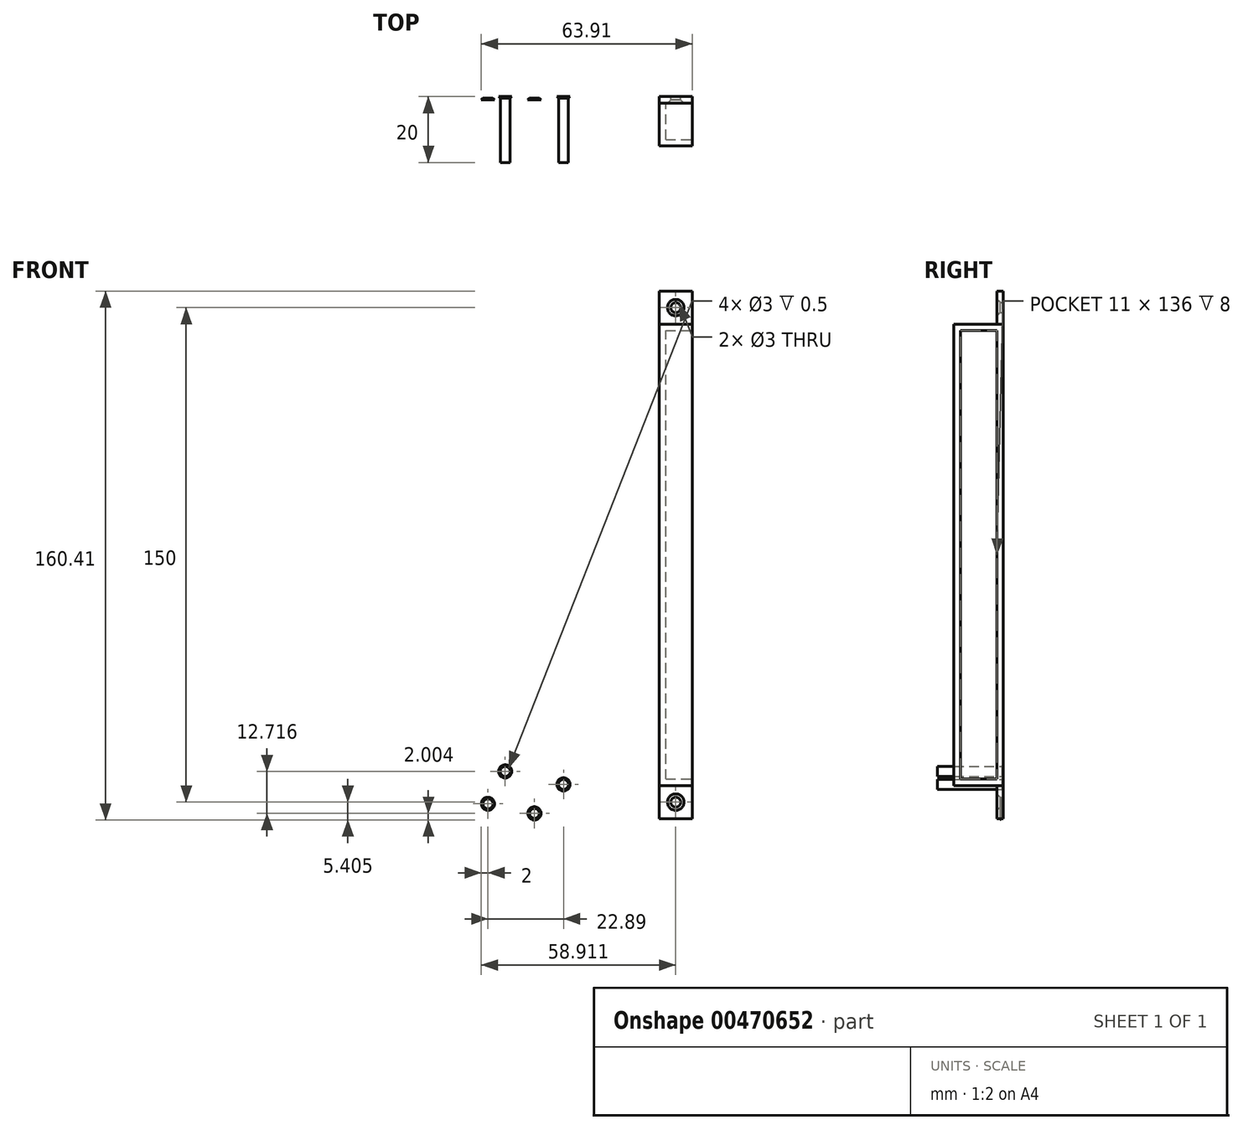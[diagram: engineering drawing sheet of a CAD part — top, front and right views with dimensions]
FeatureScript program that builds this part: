
annotation { "Feature Type Name" : "Feature", "Feature Type Description" : "" }
export const myFeature = defineFeature(function(context is Context, id is Id, definition is map)
    precondition{}
    {
        {
            var Q0;
            Q0=qCreatedBy(makeId("Front.planeOp"),FACE);
            var sketch = newSketch(context, id + "F0", { "sketchPlane" : qUnion([Q0])});
            skLineSegment(sketch, "E0.bottom", {"start": v(-57.99, -14.31) * mm, "end": v(-67.99, -14.31) * mm});
            skLineSegment(sketch, "E0.top", {"start": v(-57.99, 145.69) * mm, "end": v(-67.99, 145.69) * mm});
            skLineSegment(sketch, "E0.left", {"start": v(-57.99, -14.31) * mm, "end": v(-57.99, 145.69) * mm});
            skLineSegment(sketch, "E0.right", {"start": v(-67.99, -14.31) * mm, "end": v(-67.99, 145.69) * mm});
            skPoint(sketch, "E0.middle", {"position": v(-62.99, 65.69) * mm});
            skCircle(sketch, "E1", {"center": v(-62.99, 140.69) * mm, "radius": 1.5 * mm});
            skCircle(sketch, "E2", {"center": v(-62.99, -9.31) * mm, "radius": 1.5 * mm});
            skLineSegment(sketch, "E3", {"start": v(-67.99, -4.31) * mm, "end": v(-57.99, -4.31) * mm});
            skLineSegment(sketch, "E4", {"start": v(-67.99, 135.69) * mm, "end": v(-57.99, 135.69) * mm});
            skSolve(sketch);
        }
        {
            var Q0;
            {var subQ1=sQuery(id+"F0.wireOp",EDGE,"E0.bottom");Q0=makeQuery(id+"F0.imprint","IMPRINT",FACE,{"disambiguationData":[TD([[makeQuery(id+"F0.imprint","IMPRINT",EDGE,{"derivedFrom":subQ1}),-1.0]])]});}
            var Q1;
            {var subQ1=sQuery(id+"F0.wireOp",EDGE,"E0.top");Q1=makeQuery(id+"F0.imprint","IMPRINT",FACE,{"disambiguationData":[TD([[makeQuery(id+"F0.imprint","IMPRINT",EDGE,{"derivedFrom":subQ1}),1.0]])]});}
            extrude(context, id + "F1", {"entities" : qUnion([Q0, Q1]), "depth" : 2 * mm});
        }
        {
            var Q0;
            {var subQ0=sQuery(id+"F0.wireOp",EDGE,"E3");Q0=makeQuery(id+"F0.imprint","IMPRINT",FACE,{"disambiguationData":[TD([[makeQuery(id+"F0.imprint","IMPRINT",EDGE,{"derivedFrom":subQ0}),1.0]])]});}
            extrude(context, id + "F2", {"entities" : qUnion([Q0]), "depth" : 15 * mm});
        }
        {
            var Q0;
            Q0=makeQuery(id+"F2.opExtrude","SWEPT_FACE",FACE,{"disambiguationData":[OSD([sQuery(id+"F0.wireOp",EDGE,"E0.left")])]});
            shell(context, id + "F3", {"entities" : qUnion([Q0]), "thickness" : 2 * mm});
        }
        {
            var Q0;
            Q0=qCreatedBy(makeId("Front.planeOp"),FACE);
            var sketch = newSketch(context, id + "F4", { "sketchPlane" : qUnion([Q0])});
            skCircle(sketch, "E5", {"center": v(-97, -3.94) * mm, "radius": 1.5 * mm});
            skCircle(sketch, "E6", {"center": v(-97, -3.94) * mm, "radius": 2 * mm});
            skCircle(sketch, "E7", {"center": v(-114.68, 0) * mm, "radius": 1.5 * mm});
            skCircle(sketch, "E8", {"center": v(-114.68, 0) * mm, "radius": 2 * mm});
            skCircle(sketch, "E9", {"center": v(-105.82, -12.72) * mm, "radius": 2 * mm});
            skCircle(sketch, "E10", {"center": v(-105.82, -12.72) * mm, "radius": 1.5 * mm});
            skCircle(sketch, "E11", {"center": v(-119.9, -9.82) * mm, "radius": 2 * mm});
            skCircle(sketch, "E12", {"center": v(-119.9, -9.82) * mm, "radius": 1.5 * mm});
            skSolve(sketch);
        }
        {
            var Q0;
            Q0=makeQuery(id+"F4.imprint","IMPRINT",FACE,{"disambiguationData":[TD([[makeQuery(id+"F4.imprint","IMPRINT",EDGE,{"derivedFrom":sQuery(id+"F4.wireOp",EDGE,"E5")}),1.0]])]});
            var Q1;
            Q1=makeQuery(id+"F4.imprint","IMPRINT",FACE,{"disambiguationData":[TD([[makeQuery(id+"F4.imprint","IMPRINT",EDGE,{"derivedFrom":sQuery(id+"F4.wireOp",EDGE,"E7")}),1.0]])]});
            extrude(context, id + "F5", {"entities" : qUnion([Q0, Q1]), "depth" : 20 * mm});
        }
        {
            var Q0;
            Q0=makeQuery(id+"F4.imprint","IMPRINT",FACE,{"disambiguationData":[TD([[makeQuery(id+"F4.imprint","IMPRINT",EDGE,{"derivedFrom":sQuery(id+"F4.wireOp",EDGE,"E5")}),-1.0]])]});
            var Q1;
            Q1=makeQuery(id+"F4.imprint","IMPRINT",FACE,{"disambiguationData":[TD([[makeQuery(id+"F4.imprint","IMPRINT",EDGE,{"derivedFrom":sQuery(id+"F4.wireOp",EDGE,"E7")}),-1.0]])]});
            var Q2;
            Q2=makeQuery(id+"F4.imprint","IMPRINT",FACE,{"disambiguationData":[TD([[makeQuery(id+"F4.imprint","IMPRINT",EDGE,{"derivedFrom":sQuery(id+"F4.wireOp",EDGE,"E11")}),1.0]])]});
            var Q3;
            Q3=makeQuery(id+"F4.imprint","IMPRINT",FACE,{"disambiguationData":[TD([[makeQuery(id+"F4.imprint","IMPRINT",EDGE,{"derivedFrom":sQuery(id+"F4.wireOp",EDGE,"E9")}),1.0]])]});
            extrude(context, id + "F6", {"entities" : qUnion([Q0, Q1, Q2, Q3]), "depth" : 1 * mm});
        }
        {
            var Q0;
            Q0=makeQuery(id+"F6.opExtrude","CAP_EDGE",EDGE,{"disambiguationData":[OSD([sQuery(id+"F4.wireOp",EDGE,"E6")])],"isStart":false});
            var Q1;
            Q1=makeQuery(id+"F6.opExtrude","CAP_EDGE",EDGE,{"disambiguationData":[OSD([sQuery(id+"F4.wireOp",EDGE,"E8")])],"isStart":false});
            var Q2;
            Q2=makeQuery(id+"F6.opExtrude","CAP_EDGE",EDGE,{"disambiguationData":[OSD([sQuery(id+"F4.wireOp",EDGE,"E9")])],"isStart":true});
            var Q3;
            Q3=makeQuery(id+"F6.opExtrude","CAP_EDGE",EDGE,{"disambiguationData":[OSD([sQuery(id+"F4.wireOp",EDGE,"E11")])],"isStart":true});
            chamfer(context, id + "F7", {"entities" : qUnion([Q0, Q1, Q2, Q3]), "width" : 1 * mm, "tangentPropagation" : true});
        }
        {
            var Q0;
            Q0=makeQuery(id+"F1.opExtrude","CAP_EDGE",EDGE,{"disambiguationData":[OSD([sQuery(id+"F0.wireOp",EDGE,"E2")])],"isStart":false});
            var Q1;
            Q1=makeQuery(id+"F1.opExtrude","CAP_EDGE",EDGE,{"disambiguationData":[OSD([sQuery(id+"F0.wireOp",EDGE,"E1")])],"isStart":false});
            chamfer(context, id + "F8", {"entities" : qUnion([Q0, Q1]), "width" : 1 * mm, "tangentPropagation" : true});
        }
    });
